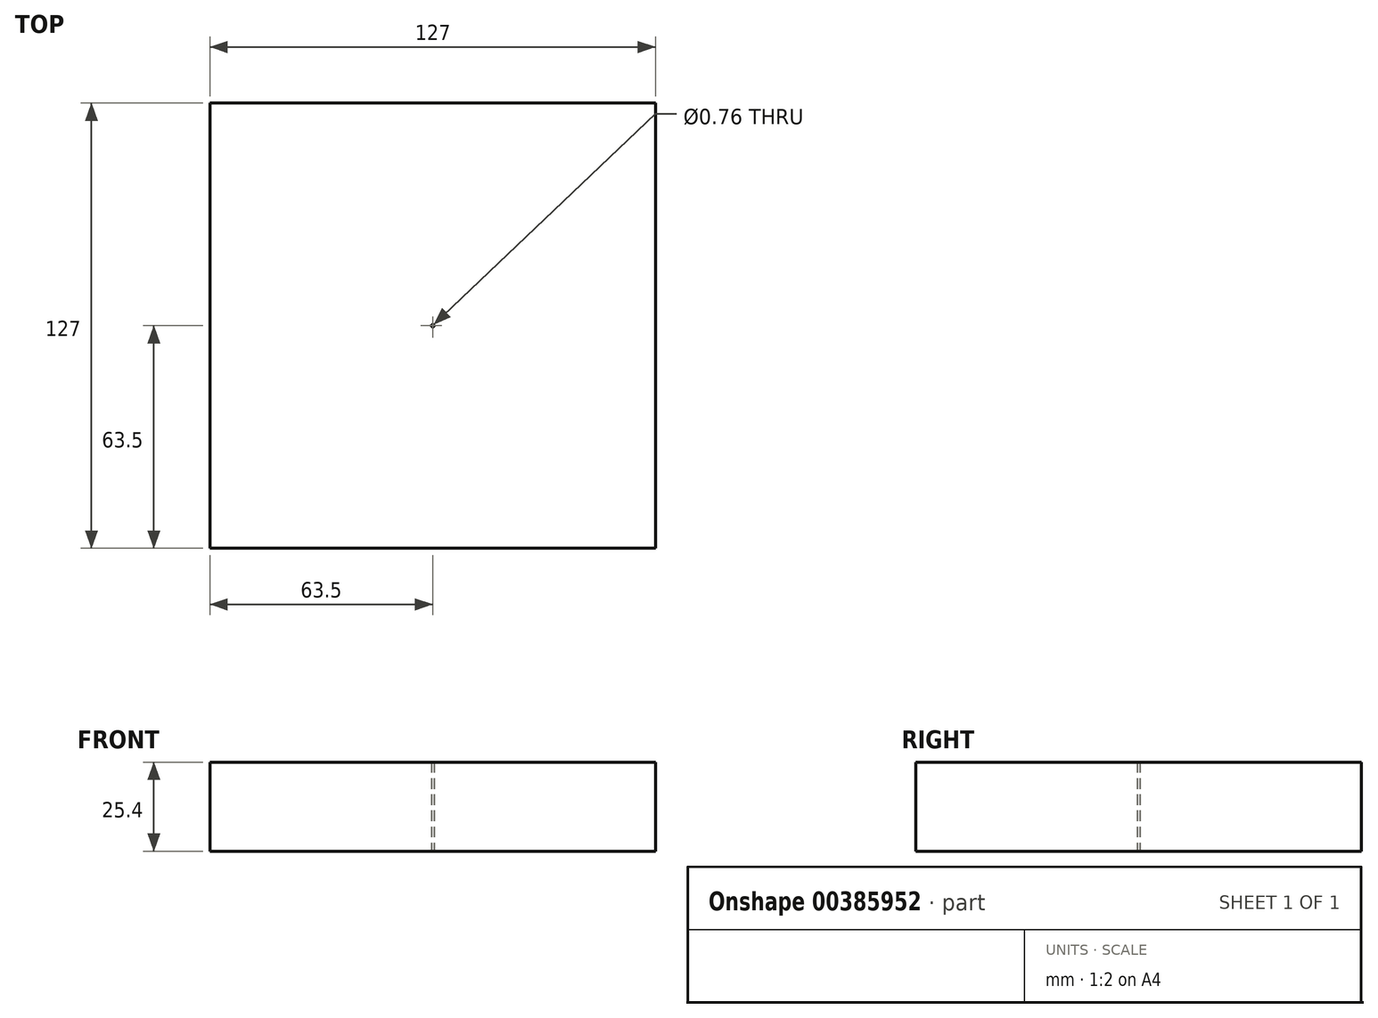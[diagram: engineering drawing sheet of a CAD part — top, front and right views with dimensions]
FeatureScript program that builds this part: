
annotation { "Feature Type Name" : "Feature", "Feature Type Description" : "" }
export const myFeature = defineFeature(function(context is Context, id is Id, definition is map)
    precondition{}
    {
        {
            var Q0;
            Q0=qCreatedBy(makeId("Top.planeOp"),FACE);
            var sketch = newSketch(context, id + "F0", { "sketchPlane" : qUnion([Q0])});
            skLineSegment(sketch, "E0.bottom", {"start": v(-63.5, 63.5) * mm, "end": v(63.5, 63.5) * mm});
            skLineSegment(sketch, "E0.top", {"start": v(-63.5, -63.5) * mm, "end": v(63.5, -63.5) * mm});
            skLineSegment(sketch, "E0.left", {"start": v(-63.5, 63.5) * mm, "end": v(-63.5, -63.5) * mm});
            skLineSegment(sketch, "E0.right", {"start": v(63.5, 63.5) * mm, "end": v(63.5, -63.5) * mm});
            skPoint(sketch, "E0.middle", {"position": v(0, 0) * mm});
            skCircle(sketch, "E1", {"center": v(0, 0) * mm, "radius": 0.38 * mm});
            skLineSegment(sketch, "E2.bottom", {"start": v(63.5, -38.1) * mm, "end": v(-63.5, -38.1) * mm});
            skLineSegment(sketch, "E2.top", {"start": v(63.5, 38.1) * mm, "end": v(-63.5, 38.1) * mm});
            skLineSegment(sketch, "E2.left", {"start": v(63.5, -38.1) * mm, "end": v(63.5, 38.1) * mm});
            skLineSegment(sketch, "E2.right", {"start": v(-63.5, -38.1) * mm, "end": v(-63.5, 38.1) * mm});
            skSolve(sketch);
        }
        {
            var Q0;
            Q0 = qSketchRegion(id + "F0", true);
            extrude(context, id + "F1", {"entities" : qUnion([Q0]), "depth" : 25.4 * mm});
        }
    });
